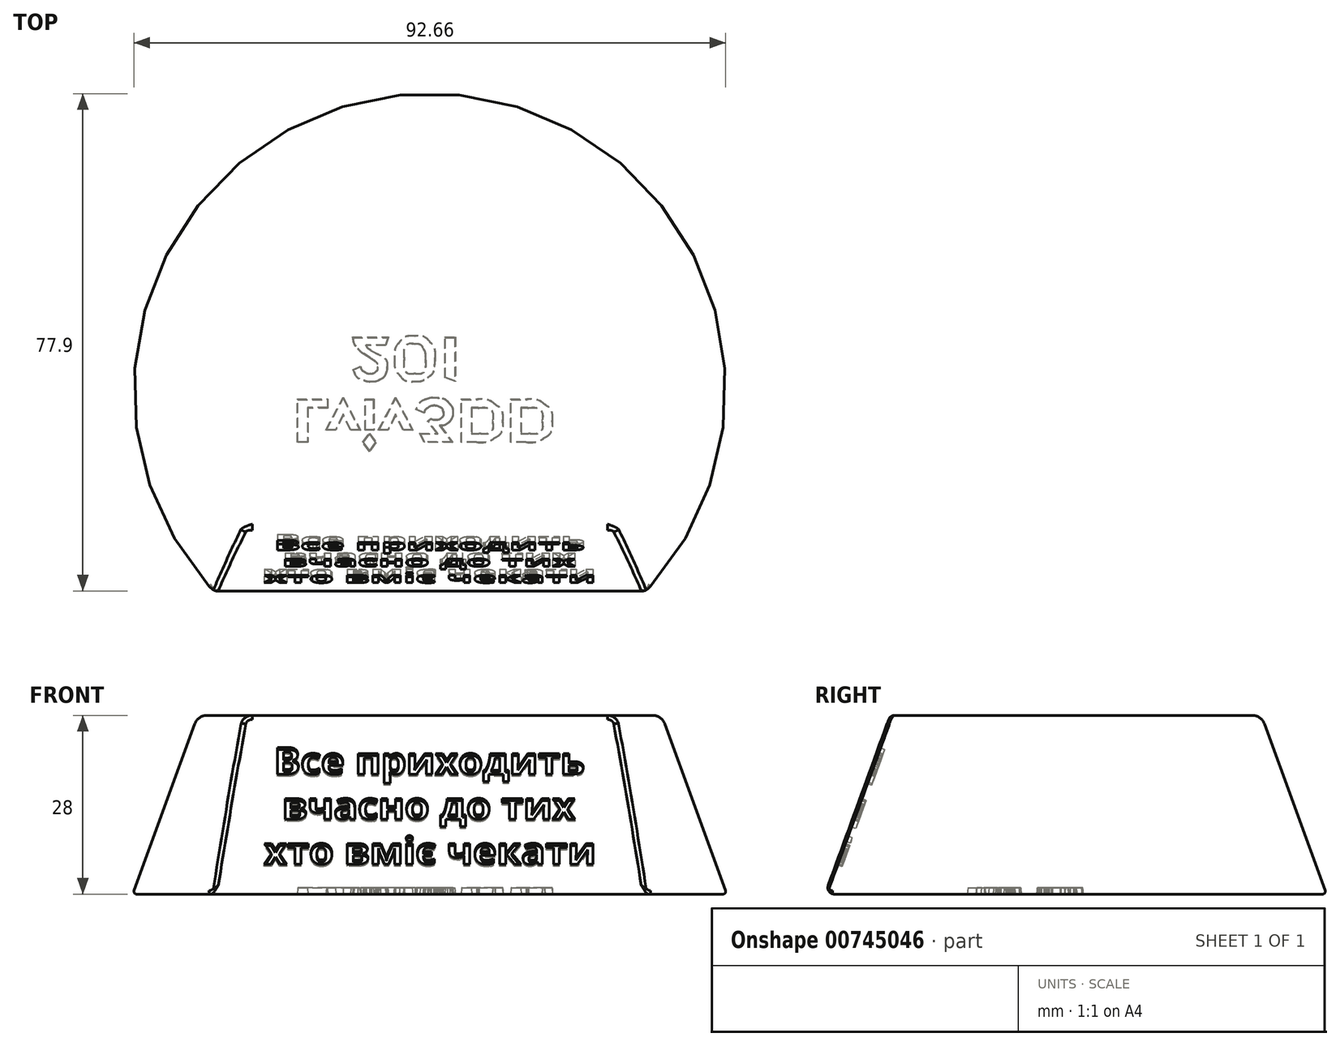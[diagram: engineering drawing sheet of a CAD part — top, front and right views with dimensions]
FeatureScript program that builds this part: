
annotation { "Feature Type Name" : "Feature", "Feature Type Description" : "" }
export const myFeature = defineFeature(function(context is Context, id is Id, definition is map)
    precondition{}
    {
        {
            var Q0;
            Q0=qCreatedBy(makeId("Top.planeOp"),FACE);
            var sketch = newSketch(context, id + "F0", { "sketchPlane" : qUnion([Q0])});
            skCircle(sketch, "E0", {"center": v(0, 0) * mm, "radius": 46.5 * mm});
            skSolve(sketch);
        }
        {
            var Q0;
            Q0=makeQuery(id+"F0.imprint","IMPRINT",FACE,{"disambiguationData":[TD([[makeQuery(id+"F0.imprint","IMPRINT",EDGE,{"derivedFrom":sQuery(id+"F0.wireOp",EDGE,"E0")}),1.0]])]});
            extrude(context, id + "F1", {"entities" : qUnion([Q0]), "depth" : 28 * mm, "offsetDistance" : 25 * mm, "hasDraft" : true, "draftAngle" : 20 * degree, "draftPullDirection" : true});
        }
        {
            var Q0;
            Q0=qCreatedBy(makeId("Right.planeOp"),FACE);
            var sketch = newSketch(context, id + "F2", { "sketchPlane" : qUnion([Q0])});
            skLineSegment(sketch, "E1", {"start": v(-46.5, 0) * mm, "end": v(-36.3, 28) * mm});
            skLineSegment(sketch, "E2", {"start": v(-36.3, 28) * mm, "end": v(-21.8, 28) * mm});
            skLineSegment(sketch, "E3", {"start": v(-21.8, 28) * mm, "end": v(-32, 0) * mm});
            skLineSegment(sketch, "E4", {"start": v(-32, 0) * mm, "end": v(-46.5, 0) * mm});
            skSolve(sketch);
        }
        {
            var Q0;
            Q0 = qSketchRegion(id + "F2", true);
            extrude(context, id + "F3", {"entities" : qUnion([Q0]), "operationType" : NewBodyOperationType.REMOVE, "endBound" : BoundingType.SYMMETRIC, "depth" : 100 * mm, "offsetDistance" : 25 * mm});
        }
        {
            var Q0;
            Q0=makeQuery(id+"F3.boolean.opBoolean","COPY",FACE,{"derivedFrom":makeQuery(id+"F3.opExtrude","SWEPT_FACE",FACE,{"disambiguationData":[OSD([sQuery(id+"F2.wireOp",EDGE,"E3")])]})});
            var sketch = newSketch(context, id + "F4", { "sketchPlane" : qUnion([Q0])});
            skLineSegment(sketch, "E5", {"start": v(0, 18.85) * mm, "end": v(0, -10.94) * mm, "construction": true});
            skText(sketch, "E6", { "text": "Все приходить вчасно", "fontName": "OpenSans-Bold.ttf"});
            skText(sketch, "E7", { "text": "до тих хто вміє чекати", "fontName": "OpenSans-Bold.ttf"});
            skText(sketch, "E8", { "text": "Все приходить", "fontName": "OpenSans-Bold.ttf"});
            skText(sketch, "E9", { "text": "вчасно до тих", "fontName": "OpenSans-Bold.ttf"});
            skText(sketch, "E10", { "text": "хто вміє чекати", "fontName": "OpenSans-Bold.ttf"});
            skLineSegment(sketch, "E11", {"start": v(0, 9.06) * mm, "end": v(0, 6.06) * mm, "construction": true});
            skLineSegment(sketch, "E12", {"start": v(0, 1.56) * mm, "end": v(0, -1.44) * mm, "construction": true});
            const initialGuessF4  = {"E6": [-0.0286, 0.04542, 1, 0, 0.0035], "E7": [-0.02909, 0.03775, 1, 0, 0.0035], "E8": [-0.02444, 0.00906, 1, 0, 0.0045], "E9": [-0.02315, 0.00156, 1, 0, 0.0045], "E10": [-0.02598, -0.00594, 1, 0, 0.0045]};
            skSetInitialGuess(sketch, initialGuessF4);
            skSolve(sketch);
        }
        {
            var Q0;
            Q0 = qSketchRegion(id + "F4", true);
            extrude(context, id + "F5", {"entities" : qUnion([Q0]), "operationType" : NewBodyOperationType.REMOVE, "oppositeDirection" : true, "depth" : 1 * mm, "offsetDistance" : 25 * mm});
        }
        {
            var Q0;
            Q0=makeQuery(id+"F1.opExtrude","CAP_EDGE",EDGE,{"disambiguationData":[OSD([sQuery(id+"F0.wireOp",EDGE,"E0")])],"isStart":false});
            var Q1;
            Q1=makeQuery(id+"F3.boolean.opBoolean","COPY",EDGE,{"derivedFrom":makeQuery(id+"F3.opExtrude","SWEPT_EDGE",EDGE,{"disambiguationData":[OSD([sQuery(id+"F2.wireOp",EDGE,"E2"),sQuery(id+"F2.wireOp",EDGE,"E3")])]})});
            fillet(context, id + "F6", {"entities" : qUnion([Q0, Q1]), "radius" : 2 * mm, "tangentPropagation" : true, "allowEdgeOverflow" : false});
        }
        {
            var Q0;
            Q0=makeQuery(id+"F1.opExtrude","CAP_EDGE",EDGE,{"disambiguationData":[OSD([sQuery(id+"F0.wireOp",EDGE,"E0")])],"isStart":true});
            var Q1;
            Q1=makeQuery(id+"F3.boolean.opBoolean","COPY",EDGE,{"derivedFrom":makeQuery(id+"F3.opExtrude","SWEPT_EDGE",EDGE,{"disambiguationData":[OSD([sQuery(id+"F2.wireOp",EDGE,"E3"),sQuery(id+"F2.wireOp",EDGE,"E4")])]})});
            fillet(context, id + "F7", {"entities" : qUnion([Q0, Q1]), "radius" : 0.4 * mm, "tangentPropagation" : true, "allowEdgeOverflow" : false});
        }
        {
            var Q0;
            Q0=makeQuery(id+"F3.boolean.opBoolean","INTERSECT",EDGE,{"disambiguationData":[OD(1.0)],"derivedFrom":[makeQuery(id+"F1.opExtrude","SWEPT_FACE",FACE,{"disambiguationData":[OSD([sQuery(id+"F0.wireOp",EDGE,"E0")])]}),makeQuery(id+"F3.opExtrude","SWEPT_FACE",FACE,{"disambiguationData":[OSD([sQuery(id+"F2.wireOp",EDGE,"E3")])]})]});
            var Q1;
            Q1=makeQuery(id+"F3.boolean.opBoolean","INTERSECT",EDGE,{"disambiguationData":[OD(0.0)],"derivedFrom":[makeQuery(id+"F1.opExtrude","SWEPT_FACE",FACE,{"disambiguationData":[OSD([sQuery(id+"F0.wireOp",EDGE,"E0")])]}),makeQuery(id+"F3.opExtrude","SWEPT_FACE",FACE,{"disambiguationData":[OSD([sQuery(id+"F2.wireOp",EDGE,"E3")])]})]});
            fillet(context, id + "F8", {"entities" : qUnion([Q0, Q1]), "radius" : 1 * mm, "tangentPropagation" : true, "allowEdgeOverflow" : false});
        }
        {
            var Q0;
            Q0=makeQuery(id+"F1.opExtrude","CAP_FACE",FACE,{"disambiguationData":[OSD([sQuery(id+"F0.wireOp",EDGE,"E0")])],"isStart":true});
            var sketch = newSketch(context, id + "F9", { "sketchPlane" : qUnion([Q0])});
            skFitSpline(sketch, "E13", {"points": [v(15.31, 2.95) * mm, v(16.8, 2.95) * mm, v(17.54, 3.63) * mm, v(17.54, 5) * mm]});
            skFitSpline(sketch, "E14", {"points": [v(17.54, 5) * mm, v(17.54, 6.25) * mm, v(16.85, 6.88) * mm, v(15.47, 6.88) * mm]});
            skLineSegment(sketch, "E15", {"start": v(14.31, 2.95) * mm, "end": v(15.31, 2.95) * mm});
            skLineSegment(sketch, "E16", {"start": v(15.47, 6.88) * mm, "end": v(14.31, 6.88) * mm});
            skLineSegment(sketch, "E17", {"start": v(14.31, 6.88) * mm, "end": v(14.31, 2.95) * mm});
            skFitSpline(sketch, "E18", {"points": [v(15.07, 8.31) * mm, v(16.3, 8.31) * mm, v(17.28, 8.07) * mm, v(17.99, 7.6) * mm]});
            skFitSpline(sketch, "E19", {"points": [v(17.99, 7.6) * mm, v(18.83, 7.03) * mm, v(19.24, 6.16) * mm, v(19.24, 4.98) * mm]});
            skFitSpline(sketch, "E20", {"points": [v(19.24, 4.98) * mm, v(19.24, 3.83) * mm, v(18.84, 2.96) * mm, v(18.04, 2.34) * mm]});
            skFitSpline(sketch, "E21", {"points": [v(18.04, 2.34) * mm, v(17.33, 1.8) * mm, v(16.38, 1.51) * mm, v(15.2, 1.51) * mm]});
            skLineSegment(sketch, "E22", {"start": v(12.65, 1.51) * mm, "end": v(12.65, 8.31) * mm});
            skLineSegment(sketch, "E23", {"start": v(12.65, 8.31) * mm, "end": v(15.07, 8.31) * mm});
            skLineSegment(sketch, "E24", {"start": v(15.2, 1.51) * mm, "end": v(12.65, 1.51) * mm});
            skFitSpline(sketch, "E25", {"points": [v(7.56, 2.95) * mm, v(9.04, 2.95) * mm, v(9.79, 3.63) * mm, v(9.79, 5) * mm]});
            skFitSpline(sketch, "E26", {"points": [v(9.79, 5) * mm, v(9.79, 6.25) * mm, v(9.1, 6.88) * mm, v(7.7, 6.88) * mm]});
            skLineSegment(sketch, "E27", {"start": v(6.56, 2.95) * mm, "end": v(7.56, 2.95) * mm});
            skLineSegment(sketch, "E28", {"start": v(7.7, 6.88) * mm, "end": v(6.56, 6.88) * mm});
            skLineSegment(sketch, "E29", {"start": v(6.56, 6.88) * mm, "end": v(6.56, 2.95) * mm});
            skFitSpline(sketch, "E30", {"points": [v(7.31, 8.31) * mm, v(8.55, 8.31) * mm, v(9.52, 8.07) * mm, v(10.23, 7.6) * mm]});
            skFitSpline(sketch, "E31", {"points": [v(10.23, 7.6) * mm, v(11.07, 7.03) * mm, v(11.49, 6.16) * mm, v(11.49, 4.98) * mm]});
            skFitSpline(sketch, "E32", {"points": [v(11.49, 4.98) * mm, v(11.49, 3.83) * mm, v(11.09, 2.96) * mm, v(10.29, 2.34) * mm]});
            skFitSpline(sketch, "E33", {"points": [v(10.29, 2.34) * mm, v(9.57, 1.8) * mm, v(8.62, 1.51) * mm, v(7.43, 1.51) * mm]});
            skLineSegment(sketch, "E34", {"start": v(4.9, 1.51) * mm, "end": v(4.9, 8.31) * mm});
            skLineSegment(sketch, "E35", {"start": v(4.9, 8.31) * mm, "end": v(7.31, 8.31) * mm});
            skLineSegment(sketch, "E36", {"start": v(7.43, 1.51) * mm, "end": v(4.9, 1.51) * mm});
            skFitSpline(sketch, "E37", {"points": [v(-0.78, 3.5) * mm, v(-0.66, 3.25) * mm, v(-0.47, 3.03) * mm, v(-0.2, 2.85) * mm]});
            skFitSpline(sketch, "E38", {"points": [v(-0.2, 2.85) * mm, v(0.07, 2.66) * mm, v(0.34, 2.56) * mm, v(0.62, 2.56) * mm]});
            skLineSegment(sketch, "E39", {"start": v(-2.22, 3.17) * mm, "end": v(-0.86, 3.7) * mm});
            skLineSegment(sketch, "E40", {"start": v(-0.86, 3.7) * mm, "end": v(-0.78, 3.5) * mm});
            skFitSpline(sketch, "E41", {"points": [v(0.76, 2.56) * mm, v(1.03, 2.56) * mm, v(1.28, 2.62) * mm, v(1.5, 2.74) * mm]});
            skFitSpline(sketch, "E42", {"points": [v(1.5, 2.74) * mm, v(1.75, 2.87) * mm, v(1.92, 3.06) * mm, v(2, 3.29) * mm]});
            skLineSegment(sketch, "E43", {"start": v(0.62, 2.56) * mm, "end": v(0.76, 2.56) * mm});
            skFitSpline(sketch, "E44", {"points": [v(2.07, 3.5) * mm, v(2.08, 3.6) * mm, v(2.09, 3.66) * mm, v(2.09, 3.71) * mm]});
            skFitSpline(sketch, "E45", {"points": [v(2.09, 3.71) * mm, v(2.09, 4.02) * mm, v(1.98, 4.26) * mm, v(1.78, 4.44) * mm]});
            skFitSpline(sketch, "E46", {"points": [v(1.78, 4.44) * mm, v(1.58, 4.62) * mm, v(1.33, 4.73) * mm, v(1.02, 4.76) * mm]});
            skFitSpline(sketch, "E47", {"points": [v(1.02, 4.76) * mm, v(0.7, 4.76) * mm, v(0.44, 4.71) * mm, v(0.24, 4.61) * mm]});
            skLineSegment(sketch, "E48", {"start": v(2, 3.29) * mm, "end": v(2.07, 3.5) * mm});
            skFitSpline(sketch, "E49", {"points": [v(1.85, 5.68) * mm, v(2.17, 5.65) * mm, v(2.48, 5.54) * mm, v(2.77, 5.35) * mm]});
            skFitSpline(sketch, "E50", {"points": [v(2.77, 5.35) * mm, v(3.07, 5.16) * mm, v(3.3, 4.93) * mm, v(3.46, 4.65) * mm]});
            skFitSpline(sketch, "E51", {"points": [v(3.46, 4.65) * mm, v(3.63, 4.35) * mm, v(3.71, 4.02) * mm, v(3.71, 3.67) * mm]});
            skFitSpline(sketch, "E52", {"points": [v(3.71, 3.67) * mm, v(3.71, 3.16) * mm, v(3.53, 2.68) * mm, v(3.16, 2.25) * mm]});
            skFitSpline(sketch, "E53", {"points": [v(3.16, 2.25) * mm, v(2.75, 1.75) * mm, v(2.2, 1.45) * mm, v(1.5, 1.35) * mm]});
            skFitSpline(sketch, "E54", {"points": [v(1.5, 1.35) * mm, v(1.2, 1.3) * mm, v(0.97, 1.29) * mm, v(0.8, 1.29) * mm]});
            skFitSpline(sketch, "E55", {"points": [v(0.8, 1.29) * mm, v(0.53, 1.29) * mm, v(0.22, 1.28) * mm, v(-0.35, 1.44) * mm]});
            skFitSpline(sketch, "E56", {"points": [v(-0.35, 1.44) * mm, v(-0.92, 1.6) * mm, v(-1.57, 2.03) * mm, v(-2.07, 2.9) * mm]});
            skLineSegment(sketch, "E57", {"start": v(0.24, 4.61) * mm, "end": v(0.13, 4.55) * mm});
            skLineSegment(sketch, "E58", {"start": v(0.13, 4.55) * mm, "end": v(-0.36, 5.02) * mm});
            skLineSegment(sketch, "E59", {"start": v(-0.36, 5.02) * mm, "end": v(1.14, 6.88) * mm});
            skLineSegment(sketch, "E60", {"start": v(1.14, 6.88) * mm, "end": v(-1.6, 6.88) * mm});
            skLineSegment(sketch, "E61", {"start": v(-1.6, 6.88) * mm, "end": v(-0.84, 8.31) * mm});
            skLineSegment(sketch, "E62", {"start": v(-0.84, 8.31) * mm, "end": v(3.59, 8.31) * mm});
            skLineSegment(sketch, "E63", {"start": v(3.59, 8.31) * mm, "end": v(1.65, 5.7) * mm});
            skLineSegment(sketch, "E64", {"start": v(1.65, 5.7) * mm, "end": v(1.85, 5.68) * mm});
            skLineSegment(sketch, "E65", {"start": v(-2.07, 2.9) * mm, "end": v(-2.22, 3.17) * mm});
            skLineSegment(sketch, "E66", {"start": v(-8.08, 6.4) * mm, "end": v(-6.5, 6.4) * mm});
            skLineSegment(sketch, "E67", {"start": v(-6.5, 6.4) * mm, "end": v(-5.35, 4.07) * mm});
            skLineSegment(sketch, "E68", {"start": v(-5.35, 4.07) * mm, "end": v(-4.18, 6.4) * mm});
            skLineSegment(sketch, "E69", {"start": v(-4.18, 6.4) * mm, "end": v(-2.62, 6.4) * mm});
            skLineSegment(sketch, "E70", {"start": v(-2.62, 6.4) * mm, "end": v(-5.35, 1.27) * mm});
            skLineSegment(sketch, "E71", {"start": v(-5.35, 1.27) * mm, "end": v(-8.08, 6.4) * mm});
            skLineSegment(sketch, "E72", {"start": v(-16.31, 6.4) * mm, "end": v(-14.73, 6.4) * mm});
            skLineSegment(sketch, "E73", {"start": v(-14.73, 6.4) * mm, "end": v(-13.58, 4.07) * mm});
            skLineSegment(sketch, "E74", {"start": v(-13.58, 4.07) * mm, "end": v(-12.42, 6.4) * mm});
            skLineSegment(sketch, "E75", {"start": v(-12.42, 6.4) * mm, "end": v(-10.85, 6.4) * mm});
            skLineSegment(sketch, "E76", {"start": v(-10.85, 6.4) * mm, "end": v(-13.58, 1.27) * mm});
            skLineSegment(sketch, "E77", {"start": v(-13.58, 1.27) * mm, "end": v(-16.31, 6.4) * mm});
            skLineSegment(sketch, "E78", {"start": v(-20.76, 1.51) * mm, "end": v(-20.76, 8.31) * mm});
            skLineSegment(sketch, "E79", {"start": v(-20.76, 8.31) * mm, "end": v(-19.1, 8.31) * mm});
            skLineSegment(sketch, "E80", {"start": v(-19.1, 8.31) * mm, "end": v(-19.1, 2.95) * mm});
            skLineSegment(sketch, "E81", {"start": v(-19.1, 2.95) * mm, "end": v(-15.96, 2.95) * mm});
            skLineSegment(sketch, "E82", {"start": v(-15.96, 2.95) * mm, "end": v(-15.96, 1.51) * mm});
            skLineSegment(sketch, "E83", {"start": v(-15.96, 1.51) * mm, "end": v(-20.76, 1.51) * mm});
            skLineSegment(sketch, "E84", {"start": v(-10.15, 1.51) * mm, "end": v(-10.15, 6.4) * mm});
            skLineSegment(sketch, "E85", {"start": v(-10.15, 6.4) * mm, "end": v(-8.77, 6.4) * mm});
            skLineSegment(sketch, "E86", {"start": v(-8.77, 6.4) * mm, "end": v(-8.77, 1.51) * mm});
            skLineSegment(sketch, "E87", {"start": v(-8.77, 1.51) * mm, "end": v(-10.15, 1.51) * mm});
            skFitSpline(sketch, "E88", {"points": [v(-12.11, -8.2) * mm, v(-12.03, -7.5) * mm, v(-11.76, -6.9) * mm, v(-11.3, -6.36) * mm]});
            skFitSpline(sketch, "E89", {"points": [v(-11.3, -6.36) * mm, v(-11, -6.02) * mm, v(-10.68, -5.75) * mm, v(-10.35, -5.54) * mm]});
            skLineSegment(sketch, "E90", {"start": v(-10.5, 8.31) * mm, "end": v(-9.45, 9.73) * mm});
            skLineSegment(sketch, "E91", {"start": v(-9.45, 9.73) * mm, "end": v(-8.43, 8.31) * mm});
            skLineSegment(sketch, "E92", {"start": v(-8.43, 8.31) * mm, "end": v(-9.45, 6.9) * mm});
            skLineSegment(sketch, "E93", {"start": v(-9.45, 6.9) * mm, "end": v(-10.5, 8.31) * mm});
            skFitSpline(sketch, "E94", {"points": [v(-9.34, -4.88) * mm, v(-8.6, -4.4) * mm, v(-8.24, -3.94) * mm, v(-8.24, -3.5) * mm]});
            skFitSpline(sketch, "E95", {"points": [v(-8.24, -3.5) * mm, v(-8.24, -3.18) * mm, v(-8.35, -2.93) * mm, v(-8.55, -2.75) * mm]});
            skFitSpline(sketch, "E96", {"points": [v(-8.55, -2.75) * mm, v(-8.77, -2.57) * mm, v(-9.04, -2.48) * mm, v(-9.37, -2.48) * mm]});
            skFitSpline(sketch, "E97", {"points": [v(-9.37, -2.48) * mm, v(-9.69, -2.48) * mm, v(-9.93, -2.59) * mm, v(-10.2, -2.75) * mm]});
            skFitSpline(sketch, "E98", {"points": [v(-10.2, -2.75) * mm, v(-10.46, -2.92) * mm, v(-10.62, -3.16) * mm, v(-10.76, -3.45) * mm]});
            skLineSegment(sketch, "E99", {"start": v(-10.35, -5.54) * mm, "end": v(-10.3, -5.52) * mm});
            skLineSegment(sketch, "E100", {"start": v(-10.3, -5.52) * mm, "end": v(-9.34, -4.88) * mm});
            skFitSpline(sketch, "E101", {"points": [v(-11.93, -2.81) * mm, v(-11.54, -2) * mm, v(-10.89, -1.55) * mm, v(-10.34, -1.39) * mm]});
            skFitSpline(sketch, "E102", {"points": [v(-10.34, -1.39) * mm, v(-9.8, -1.23) * mm, v(-9.55, -1.2) * mm, v(-9.12, -1.2) * mm]});
            skFitSpline(sketch, "E103", {"points": [v(-9.12, -1.2) * mm, v(-8.62, -1.22) * mm, v(-8.14, -1.33) * mm, v(-7.7, -1.58) * mm]});
            skFitSpline(sketch, "E104", {"points": [v(-7.7, -1.58) * mm, v(-7.2, -1.85) * mm, v(-6.89, -2.3) * mm, v(-6.76, -2.66) * mm]});
            skFitSpline(sketch, "E105", {"points": [v(-6.76, -2.66) * mm, v(-6.63, -3.01) * mm, v(-6.6, -3.27) * mm, v(-6.6, -3.46) * mm]});
            skFitSpline(sketch, "E106", {"points": [v(-6.6, -3.46) * mm, v(-6.6, -4.3) * mm, v(-7.1, -4.99) * mm, v(-8.1, -5.54) * mm]});
            skLineSegment(sketch, "E107", {"start": v(-10.76, -3.45) * mm, "end": v(-10.85, -3.65) * mm});
            skLineSegment(sketch, "E108", {"start": v(-10.85, -3.65) * mm, "end": v(-12.06, -3.1) * mm});
            skLineSegment(sketch, "E109", {"start": v(-12.06, -3.1) * mm, "end": v(-11.93, -2.81) * mm});
            skFitSpline(sketch, "E110", {"points": [v(-9.21, -6.16) * mm, v(-9.56, -6.4) * mm, v(-9.78, -6.62) * mm, v(-9.88, -6.86) * mm]});
            skLineSegment(sketch, "E111", {"start": v(-8.1, -5.54) * mm, "end": v(-9.1, -6.07) * mm});
            skLineSegment(sketch, "E112", {"start": v(-9.1, -6.07) * mm, "end": v(-9.21, -6.16) * mm});
            skFitSpline(sketch, "E113", {"points": [v(-5.58, -4.8) * mm, v(-5.58, -3.72) * mm, v(-5.31, -2.87) * mm, v(-4.78, -2.24) * mm]});
            skFitSpline(sketch, "E114", {"points": [v(-4.78, -2.24) * mm, v(-4.21, -1.56) * mm, v(-3.4, -1.22) * mm, v(-2.34, -1.22) * mm]});
            skFitSpline(sketch, "E115", {"points": [v(-2.34, -1.22) * mm, v(-1.58, -1.22) * mm, v(-0.9, -1.43) * mm, v(-0.32, -1.84) * mm]});
            skFitSpline(sketch, "E116", {"points": [v(-0.32, -1.84) * mm, v(0.32, -2.29) * mm, v(0.69, -2.87) * mm, v(0.78, -3.6) * mm]});
            skFitSpline(sketch, "E117", {"points": [v(0.78, -3.6) * mm, v(0.86, -4.18) * mm, v(0.9, -4.6) * mm, v(0.9, -4.88) * mm]});
            skFitSpline(sketch, "E118", {"points": [v(0.9, -4.88) * mm, v(0.9, -5.95) * mm, v(0.62, -6.79) * mm, v(0.08, -7.4) * mm]});
            skFitSpline(sketch, "E119", {"points": [v(0.08, -7.4) * mm, v(-0.5, -8.07) * mm, v(-1.3, -8.4) * mm, v(-2.34, -8.4) * mm]});
            skFitSpline(sketch, "E120", {"points": [v(-2.34, -8.4) * mm, v(-3.41, -8.4) * mm, v(-4.23, -8.06) * mm, v(-4.8, -7.39) * mm]});
            skFitSpline(sketch, "E121", {"points": [v(-4.8, -7.39) * mm, v(-5.31, -6.76) * mm, v(-5.58, -5.9) * mm, v(-5.58, -4.8) * mm]});
            skLineSegment(sketch, "E122", {"start": v(-9.88, -6.86) * mm, "end": v(-6.9, -6.86) * mm});
            skLineSegment(sketch, "E123", {"start": v(-6.9, -6.86) * mm, "end": v(-6.43, -8.2) * mm});
            skLineSegment(sketch, "E124", {"start": v(-6.43, -8.2) * mm, "end": v(-12.11, -8.2) * mm});
            skFitSpline(sketch, "E125", {"points": [v(-3.92, -4.8) * mm, v(-3.92, -6.34) * mm, v(-3.4, -7.1) * mm, v(-2.34, -7.1) * mm]});
            skFitSpline(sketch, "E126", {"points": [v(-2.34, -7.1) * mm, v(-1.77, -7.1) * mm, v(-1.35, -6.86) * mm, v(-1.08, -6.38) * mm]});
            skFitSpline(sketch, "E127", {"points": [v(-1.08, -6.38) * mm, v(-0.87, -6) * mm, v(-0.76, -5.5) * mm, v(-0.76, -4.88) * mm]});
            skFitSpline(sketch, "E128", {"points": [v(-0.76, -4.88) * mm, v(-0.76, -3.3) * mm, v(-1.29, -2.51) * mm, v(-2.34, -2.51) * mm]});
            skFitSpline(sketch, "E129", {"points": [v(-2.34, -2.51) * mm, v(-3.4, -2.51) * mm, v(-3.92, -3.28) * mm, v(-3.92, -4.8) * mm]});
            skLineSegment(sketch, "E130", {"start": v(2.35, -8.2) * mm, "end": v(2.35, -1.8) * mm});
            skLineSegment(sketch, "E131", {"start": v(2.35, -1.8) * mm, "end": v(4.01, -1.22) * mm});
            skLineSegment(sketch, "E132", {"start": v(4.01, -1.22) * mm, "end": v(4.01, -8.2) * mm});
            skLineSegment(sketch, "E133", {"start": v(4.01, -8.2) * mm, "end": v(2.35, -8.2) * mm});
            skFitSpline(sketch, "E134", {"points": [v(10.18, -3.3) * mm, v(9.48, -4.25) * mm, v(8.95, -5.4) * mm, v(8.56, -6.78) * mm]});
            skFitSpline(sketch, "E135", {"points": [v(8.56, -6.78) * mm, v(8.47, -7.1) * mm, v(8.4, -7.39) * mm, v(8.35, -7.66) * mm]});
            skLineSegment(sketch, "E136", {"start": v(5.15, -2.84) * mm, "end": v(5.52, -1.4) * mm});
            skLineSegment(sketch, "E137", {"start": v(5.52, -1.4) * mm, "end": v(10.6, -1.4) * mm});
            skLineSegment(sketch, "E138", {"start": v(10.6, -1.4) * mm, "end": v(10.6, -2.73) * mm});
            skLineSegment(sketch, "E139", {"start": v(10.6, -2.73) * mm, "end": v(10.18, -3.3) * mm});
            skFitSpline(sketch, "E140", {"points": [v(6.57, -7.84) * mm, v(6.75, -6.65) * mm, v(7, -6.05) * mm, v(7.57, -4.96) * mm]});
            skFitSpline(sketch, "E141", {"points": [v(7.57, -4.96) * mm, v(8.13, -3.87) * mm, v(8.01, -4.07) * mm, v(8.84, -2.84) * mm]});
            skLineSegment(sketch, "E142", {"start": v(8.35, -7.66) * mm, "end": v(8.25, -8.2) * mm});
            skLineSegment(sketch, "E143", {"start": v(8.25, -8.2) * mm, "end": v(6.51, -8.2) * mm});
            skLineSegment(sketch, "E144", {"start": v(6.51, -8.2) * mm, "end": v(6.57, -7.84) * mm});
            skLineSegment(sketch, "E145", {"start": v(8.84, -2.84) * mm, "end": v(5.15, -2.84) * mm});
            skSolve(sketch);
        }
        {
            var Q0;
            Q0 = qSketchRegion(id + "F9", true);
            extrude(context, id + "F10", {"entities" : qUnion([Q0]), "operationType" : NewBodyOperationType.REMOVE, "oppositeDirection" : true, "depth" : 1 * mm, "offsetDistance" : 25 * mm, "hasDraft" : true, "draftAngle" : 5 * degree, "draftPullDirection" : true});
        }
    });
